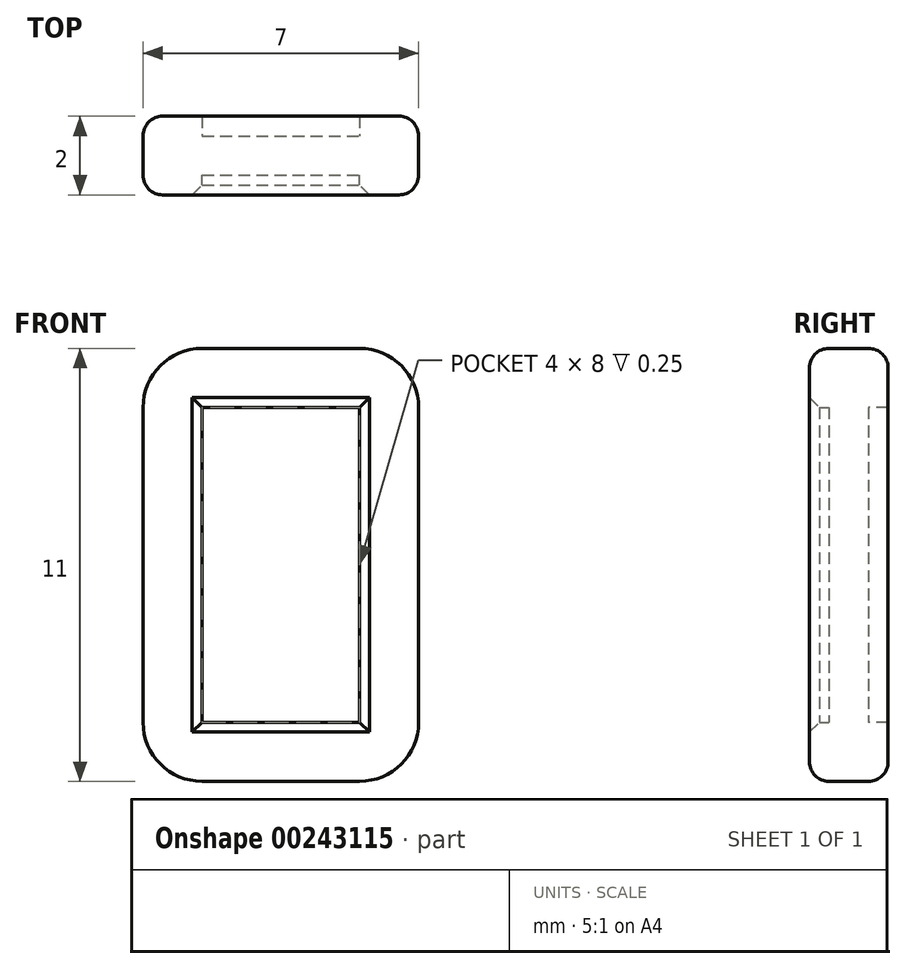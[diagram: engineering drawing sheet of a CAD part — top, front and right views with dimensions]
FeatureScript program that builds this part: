
annotation { "Feature Type Name" : "Feature", "Feature Type Description" : "" }
export const myFeature = defineFeature(function(context is Context, id is Id, definition is map)
    precondition{}
    {
        {
            var Q0;
            Q0=qCreatedBy(makeId("Front.planeOp"),FACE);
            var sketch = newSketch(context, id + "F0", { "sketchPlane" : qUnion([Q0])});
            skLineSegment(sketch, "E0", {"start": v(0, 0) * mm, "end": v(6, 0) * mm});
            skLineSegment(sketch, "E1", {"start": v(6, 0) * mm, "end": v(6, 10) * mm});
            skLineSegment(sketch, "E2", {"start": v(6, 10) * mm, "end": v(0, 10) * mm});
            skLineSegment(sketch, "E3", {"start": v(0, 10) * mm, "end": v(0, 0) * mm});
            skSolve(sketch);
        }
        {
            var Q0;
            Q0=makeQuery(id+"F0.imprint","IMPRINT",FACE,{"disambiguationData":[TD([[makeQuery(id+"F0.imprint","IMPRINT",EDGE,{"derivedFrom":sQuery(id+"F0.wireOp",EDGE,"E0")}),1.0]])]});
            extrude(context, id + "F1", {"entities" : qUnion([Q0]), "depth" : 1 * mm});
        }
        {
            var Q0;
            Q0=makeQuery(id+"F1.opExtrude","SWEPT_EDGE",EDGE,{"disambiguationData":[OSD([sQuery(id+"F0.wireOp",EDGE,"E2"),sQuery(id+"F0.wireOp",EDGE,"E3")])]});
            var Q1;
            Q1=makeQuery(id+"F1.opExtrude","SWEPT_EDGE",EDGE,{"disambiguationData":[OSD([sQuery(id+"F0.wireOp",EDGE,"E0"),sQuery(id+"F0.wireOp",EDGE,"E3")])]});
            var Q2;
            Q2=makeQuery(id+"F1.opExtrude","SWEPT_EDGE",EDGE,{"disambiguationData":[OSD([sQuery(id+"F0.wireOp",EDGE,"E0"),sQuery(id+"F0.wireOp",EDGE,"E1")])]});
            var Q3;
            Q3=makeQuery(id+"F1.opExtrude","SWEPT_EDGE",EDGE,{"disambiguationData":[OSD([sQuery(id+"F0.wireOp",EDGE,"E1"),sQuery(id+"F0.wireOp",EDGE,"E2")])]});
            fillet(context, id + "F2", {"entities" : qUnion([Q0, Q1, Q2, Q3]), "radius" : 1 * mm, "tangentPropagation" : true, "allowEdgeOverflow" : false});
        }
        {
            var Q0;
            Q0=qCreatedBy(makeId("Top.planeOp"),FACE);
            cPlane(context, id + "F3", {"entities" : qUnion([Q0]), "cplaneType" : CPlaneType.OFFSET, "offset" : 1 * mm, "width" : 150 * mm, "height" : 150 * mm});
        }
        {
            var Q0;
            Q0=qCreatedBy(id+"F3.planeOp",FACE);
            var sketch = newSketch(context, id + "F4", { "sketchPlane" : qUnion([Q0])});
            skPoint(sketch, "E4.0", {"position": v(6, -1) * mm});
            skPoint(sketch, "E4.1", {"position": v(6, 0) * mm});
            skPoint(sketch, "E4.2", {"position": v(5, -1) * mm});
            skPoint(sketch, "E4.3", {"position": v(5, 0) * mm});
            skLineSegment(sketch, "E5", {"start": v(5, -1) * mm, "end": v(6, -1) * mm});
            skLineSegment(sketch, "E6", {"start": v(6, 0) * mm, "end": v(6, -1) * mm});
            skLineSegment(sketch, "E7", {"start": v(6, 0) * mm, "end": v(5, 0) * mm});
            skLineSegment(sketch, "E8.0", {"start": v(6.5, 0.5) * mm, "end": v(5, 0.5) * mm});
            skLineSegment(sketch, "E8.1", {"start": v(6.5, 0.5) * mm, "end": v(6.5, -1.5) * mm});
            skLineSegment(sketch, "E8.2", {"start": v(5, -1.5) * mm, "end": v(6.5, -1.5) * mm});
            skLineSegment(sketch, "E9", {"start": v(5, -1.5) * mm, "end": v(5, -1) * mm});
            skLineSegment(sketch, "E10", {"start": v(5, 0.5) * mm, "end": v(5, 0) * mm});
            skSolve(sketch);
        }
        {
            var Q0;
            Q0=makeQuery(id+"F4.imprint","IMPRINT",FACE,{"disambiguationData":[TD([[makeQuery(id+"F4.imprint","IMPRINT",EDGE,{"derivedFrom":sQuery(id+"F4.wireOp",EDGE,"E5")}),-1.0]])]});
            var Q1;
            Q1=makeQuery(id+"F1.opExtrude","CAP_EDGE",EDGE,{"disambiguationData":[OSD([sQuery(id+"F0.wireOp",EDGE,"E1")])],"isStart":false});
            var Q2;
            {var subQ0=sQuery(id+"F0.wireOp",EDGE,"E2");var subQ1=sQuery(id+"F0.wireOp",EDGE,"E1");Q2=makeQuery(id+"F2.opFillet","BLEND_EDGE",EDGE,{"blendedFrom":[makeQuery(id+"F1.opExtrude","SWEPT_EDGE",EDGE,{"disambiguationData":[OSD([subQ1,subQ0])]}),makeQuery(id+"F1.opExtrude","CAP_FACE",FACE,{"disambiguationData":[OSD([sQuery(id+"F0.wireOp",EDGE,"E0"),subQ1,subQ0,sQuery(id+"F0.wireOp",EDGE,"E3")])],"isStart":false})],"blendedInto":[makeQuery(id+"F1.opExtrude","CAP_FACE",FACE,{"disambiguationData":[OSD([sQuery(id+"F0.wireOp",EDGE,"E0"),subQ1,subQ0,sQuery(id+"F0.wireOp",EDGE,"E3")])],"isStart":false})]});}
            var Q3;
            Q3=makeQuery(id+"F1.opExtrude","CAP_EDGE",EDGE,{"disambiguationData":[OSD([sQuery(id+"F0.wireOp",EDGE,"E2")])],"isStart":false});
            var Q4;
            {var subQ0=sQuery(id+"F0.wireOp",EDGE,"E3");var subQ1=sQuery(id+"F0.wireOp",EDGE,"E2");Q4=makeQuery(id+"F2.opFillet","BLEND_EDGE",EDGE,{"blendedFrom":[makeQuery(id+"F1.opExtrude","SWEPT_EDGE",EDGE,{"disambiguationData":[OSD([subQ1,subQ0])]}),makeQuery(id+"F1.opExtrude","CAP_FACE",FACE,{"disambiguationData":[OSD([sQuery(id+"F0.wireOp",EDGE,"E0"),sQuery(id+"F0.wireOp",EDGE,"E1"),subQ1,subQ0])],"isStart":false})],"blendedInto":[makeQuery(id+"F1.opExtrude","CAP_FACE",FACE,{"disambiguationData":[OSD([sQuery(id+"F0.wireOp",EDGE,"E0"),sQuery(id+"F0.wireOp",EDGE,"E1"),subQ1,subQ0])],"isStart":false})]});}
            var Q5;
            Q5=makeQuery(id+"F1.opExtrude","CAP_EDGE",EDGE,{"disambiguationData":[OSD([sQuery(id+"F0.wireOp",EDGE,"E3")])],"isStart":false});
            var Q6;
            {var subQ0=sQuery(id+"F0.wireOp",EDGE,"E3");var subQ1=sQuery(id+"F0.wireOp",EDGE,"E0");Q6=makeQuery(id+"F2.opFillet","BLEND_EDGE",EDGE,{"blendedFrom":[makeQuery(id+"F1.opExtrude","SWEPT_EDGE",EDGE,{"disambiguationData":[OSD([subQ1,subQ0])]}),makeQuery(id+"F1.opExtrude","CAP_FACE",FACE,{"disambiguationData":[OSD([subQ1,sQuery(id+"F0.wireOp",EDGE,"E1"),sQuery(id+"F0.wireOp",EDGE,"E2"),subQ0])],"isStart":false})],"blendedInto":[makeQuery(id+"F1.opExtrude","CAP_FACE",FACE,{"disambiguationData":[OSD([subQ1,sQuery(id+"F0.wireOp",EDGE,"E1"),sQuery(id+"F0.wireOp",EDGE,"E2"),subQ0])],"isStart":false})]});}
            var Q7;
            Q7=makeQuery(id+"F1.opExtrude","CAP_EDGE",EDGE,{"disambiguationData":[OSD([sQuery(id+"F0.wireOp",EDGE,"E0")])],"isStart":false});
            var Q8;
            {var subQ0=sQuery(id+"F0.wireOp",EDGE,"E1");var subQ1=sQuery(id+"F0.wireOp",EDGE,"E0");Q8=makeQuery(id+"F2.opFillet","BLEND_EDGE",EDGE,{"blendedFrom":[makeQuery(id+"F1.opExtrude","SWEPT_EDGE",EDGE,{"disambiguationData":[OSD([subQ1,subQ0])]}),makeQuery(id+"F1.opExtrude","CAP_FACE",FACE,{"disambiguationData":[OSD([subQ1,subQ0,sQuery(id+"F0.wireOp",EDGE,"E2"),sQuery(id+"F0.wireOp",EDGE,"E3")])],"isStart":false})],"blendedInto":[makeQuery(id+"F1.opExtrude","CAP_FACE",FACE,{"disambiguationData":[OSD([subQ1,subQ0,sQuery(id+"F0.wireOp",EDGE,"E2"),sQuery(id+"F0.wireOp",EDGE,"E3")])],"isStart":false})]});}
            sweep(context, id + "F5", {"operationType" : NewBodyOperationType.ADD, "profiles" : qUnion([Q0]), "path" : qUnion([Q1, Q2, Q3, Q4, Q5, Q6, Q7, Q8])});
        }
        {
            var Q0;
            {var subQ0=sQuery(id+"F4.wireOp",EDGE,"E8.2");var subQ1=sQuery(id+"F4.wireOp",EDGE,"E8.1");var subQ2=sQuery(id+"F0.wireOp",EDGE,"E3");var subQ3=sQuery(id+"F0.wireOp",EDGE,"E2");var subQ4=sQuery(id+"F0.wireOp",EDGE,"E1");var subQ5=sQuery(id+"F0.wireOp",EDGE,"E0");Q0=makeQuery(id+"F5.opSweep","SWEPT_EDGE",EDGE,{"disambiguationData":[OSD([subQ5,subQ4,subQ3,subQ2,subQ1,subQ0]),TDD([makeQuery(id+"F2.opFillet","BLEND_EDGE",EDGE,{"blendedFrom":[makeQuery(id+"F1.opExtrude","SWEPT_EDGE",EDGE,{"disambiguationData":[OSD([subQ4,subQ3])]}),makeQuery(id+"F1.opExtrude","CAP_FACE",FACE,{"disambiguationData":[OSD([subQ5,subQ4,subQ3,subQ2])],"isStart":false})],"blendedInto":[makeQuery(id+"F1.opExtrude","CAP_FACE",FACE,{"disambiguationData":[OSD([subQ5,subQ4,subQ3,subQ2])],"isStart":false})]}),makeQuery(id+"F4.imprint","INTERSECT",VERTEX,{"derivedFrom":[subQ1,subQ0]})])]});}
            var Q1;
            {var subQ0=sQuery(id+"F4.wireOp",EDGE,"E8.1");var subQ1=sQuery(id+"F4.wireOp",EDGE,"E8.0");var subQ2=sQuery(id+"F0.wireOp",EDGE,"E3");var subQ3=sQuery(id+"F0.wireOp",EDGE,"E2");var subQ4=sQuery(id+"F0.wireOp",EDGE,"E1");var subQ5=sQuery(id+"F0.wireOp",EDGE,"E0");Q1=makeQuery(id+"F5.opSweep","SWEPT_EDGE",EDGE,{"disambiguationData":[OSD([subQ5,subQ4,subQ3,subQ2,subQ1,subQ0]),TDD([makeQuery(id+"F2.opFillet","BLEND_EDGE",EDGE,{"blendedFrom":[makeQuery(id+"F1.opExtrude","SWEPT_EDGE",EDGE,{"disambiguationData":[OSD([subQ4,subQ3])]}),makeQuery(id+"F1.opExtrude","CAP_FACE",FACE,{"disambiguationData":[OSD([subQ5,subQ4,subQ3,subQ2])],"isStart":false})],"blendedInto":[makeQuery(id+"F1.opExtrude","CAP_FACE",FACE,{"disambiguationData":[OSD([subQ5,subQ4,subQ3,subQ2])],"isStart":false})]}),makeQuery(id+"F4.imprint","INTERSECT",VERTEX,{"derivedFrom":[subQ1,subQ0]})])]});}
            var Q2;
            {var subQ0=sQuery(id+"F4.wireOp",EDGE,"E8.2");var subQ1=sQuery(id+"F4.wireOp",EDGE,"E8.1");var subQ2=sQuery(id+"F0.wireOp",EDGE,"E3");var subQ3=sQuery(id+"F0.wireOp",EDGE,"E2");var subQ4=sQuery(id+"F0.wireOp",EDGE,"E1");var subQ5=sQuery(id+"F0.wireOp",EDGE,"E0");Q2=makeQuery(id+"F5.opSweep","SWEPT_EDGE",EDGE,{"disambiguationData":[OSD([subQ5,subQ4,subQ3,subQ2,subQ1,subQ0]),TDD([makeQuery(id+"F2.opFillet","BLEND_EDGE",EDGE,{"blendedFrom":[makeQuery(id+"F1.opExtrude","SWEPT_EDGE",EDGE,{"disambiguationData":[OSD([subQ3,subQ2])]}),makeQuery(id+"F1.opExtrude","CAP_FACE",FACE,{"disambiguationData":[OSD([subQ5,subQ4,subQ3,subQ2])],"isStart":false})],"blendedInto":[makeQuery(id+"F1.opExtrude","CAP_FACE",FACE,{"disambiguationData":[OSD([subQ5,subQ4,subQ3,subQ2])],"isStart":false})]}),makeQuery(id+"F4.imprint","INTERSECT",VERTEX,{"derivedFrom":[subQ1,subQ0]})])]});}
            var Q3;
            {var subQ0=sQuery(id+"F4.wireOp",EDGE,"E8.1");var subQ1=sQuery(id+"F0.wireOp",EDGE,"E3");var subQ2=sQuery(id+"F0.wireOp",EDGE,"E2");var subQ3=sQuery(id+"F0.wireOp",EDGE,"E1");var subQ4=sQuery(id+"F0.wireOp",EDGE,"E0");Q3=makeQuery(id+"F5.opSweep","SWEPT_FACE",FACE,{"disambiguationData":[OSD([subQ4,subQ3,subQ2,subQ1,subQ0]),TDD([makeQuery(id+"F2.opFillet","BLEND_EDGE",EDGE,{"blendedFrom":[makeQuery(id+"F1.opExtrude","SWEPT_EDGE",EDGE,{"disambiguationData":[OSD([subQ2,subQ1])]}),makeQuery(id+"F1.opExtrude","CAP_FACE",FACE,{"disambiguationData":[OSD([subQ4,subQ3,subQ2,subQ1])],"isStart":false})],"blendedInto":[makeQuery(id+"F1.opExtrude","CAP_FACE",FACE,{"disambiguationData":[OSD([subQ4,subQ3,subQ2,subQ1])],"isStart":false})]}),makeQuery(id+"F4.imprint","IMPRINT",EDGE,{"derivedFrom":subQ0})])]});}
            var Q4;
            {var subQ0=sQuery(id+"F4.wireOp",EDGE,"E8.2");var subQ1=sQuery(id+"F4.wireOp",EDGE,"E8.1");var subQ2=sQuery(id+"F0.wireOp",EDGE,"E3");var subQ3=sQuery(id+"F0.wireOp",EDGE,"E2");var subQ4=sQuery(id+"F0.wireOp",EDGE,"E1");var subQ5=sQuery(id+"F0.wireOp",EDGE,"E0");Q4=makeQuery(id+"F5.opSweep","SWEPT_EDGE",EDGE,{"disambiguationData":[OSD([subQ5,subQ4,subQ3,subQ2,subQ1,subQ0]),TDD([makeQuery(id+"F2.opFillet","BLEND_EDGE",EDGE,{"blendedFrom":[makeQuery(id+"F1.opExtrude","SWEPT_EDGE",EDGE,{"disambiguationData":[OSD([subQ5,subQ4])]}),makeQuery(id+"F1.opExtrude","CAP_FACE",FACE,{"disambiguationData":[OSD([subQ5,subQ4,subQ3,subQ2])],"isStart":false})],"blendedInto":[makeQuery(id+"F1.opExtrude","CAP_FACE",FACE,{"disambiguationData":[OSD([subQ5,subQ4,subQ3,subQ2])],"isStart":false})]}),makeQuery(id+"F4.imprint","INTERSECT",VERTEX,{"derivedFrom":[subQ1,subQ0]})])]});}
            var Q5;
            {var subQ0=sQuery(id+"F4.wireOp",EDGE,"E8.1");var subQ1=sQuery(id+"F4.wireOp",EDGE,"E8.0");var subQ2=sQuery(id+"F0.wireOp",EDGE,"E3");var subQ3=sQuery(id+"F0.wireOp",EDGE,"E2");var subQ4=sQuery(id+"F0.wireOp",EDGE,"E1");var subQ5=sQuery(id+"F0.wireOp",EDGE,"E0");Q5=makeQuery(id+"F5.opSweep","SWEPT_EDGE",EDGE,{"disambiguationData":[OSD([subQ5,subQ4,subQ3,subQ2,subQ1,subQ0]),TDD([makeQuery(id+"F2.opFillet","BLEND_EDGE",EDGE,{"blendedFrom":[makeQuery(id+"F1.opExtrude","SWEPT_EDGE",EDGE,{"disambiguationData":[OSD([subQ5,subQ4])]}),makeQuery(id+"F1.opExtrude","CAP_FACE",FACE,{"disambiguationData":[OSD([subQ5,subQ4,subQ3,subQ2])],"isStart":false})],"blendedInto":[makeQuery(id+"F1.opExtrude","CAP_FACE",FACE,{"disambiguationData":[OSD([subQ5,subQ4,subQ3,subQ2])],"isStart":false})]}),makeQuery(id+"F4.imprint","INTERSECT",VERTEX,{"derivedFrom":[subQ1,subQ0]})])]});}
            var Q6;
            Q6=makeQuery(id+"F5.opSweep","MID_CAP_EDGE",EDGE,{"disambiguationData":[OSD([sQuery(id+"F0.wireOp",EDGE,"E0"),sQuery(id+"F0.wireOp",EDGE,"E1"),sQuery(id+"F0.wireOp",EDGE,"E2"),sQuery(id+"F0.wireOp",EDGE,"E3"),sQuery(id+"F4.wireOp",EDGE,"E8.1")])],"capPos":4.0});
            var Q7;
            {var subQ0=sQuery(id+"F4.wireOp",EDGE,"E8.1");var subQ1=sQuery(id+"F0.wireOp",EDGE,"E3");var subQ2=sQuery(id+"F0.wireOp",EDGE,"E2");var subQ3=sQuery(id+"F0.wireOp",EDGE,"E1");var subQ4=sQuery(id+"F0.wireOp",EDGE,"E0");Q7=makeQuery(id+"F5.opSweep","SWEPT_FACE",FACE,{"disambiguationData":[OSD([subQ4,subQ3,subQ2,subQ1,subQ0]),TDD([makeQuery(id+"F2.opFillet","BLEND_EDGE",EDGE,{"blendedFrom":[makeQuery(id+"F1.opExtrude","SWEPT_EDGE",EDGE,{"disambiguationData":[OSD([subQ4,subQ1])]}),makeQuery(id+"F1.opExtrude","CAP_FACE",FACE,{"disambiguationData":[OSD([subQ4,subQ3,subQ2,subQ1])],"isStart":false})],"blendedInto":[makeQuery(id+"F1.opExtrude","CAP_FACE",FACE,{"disambiguationData":[OSD([subQ4,subQ3,subQ2,subQ1])],"isStart":false})]}),makeQuery(id+"F4.imprint","IMPRINT",EDGE,{"derivedFrom":subQ0})])]});}
            fillet(context, id + "F6", {"entities" : qUnion([Q0, Q1, Q2, Q3, Q4, Q5, Q6, Q7]), "radius" : 0.5 * mm, "tangentPropagation" : true, "allowEdgeOverflow" : false});
        }
        {
            var Q0;
            Q0=makeQuery(id+"F5.opSweep","SWEPT_EDGE",EDGE,{"disambiguationData":[OSD([sQuery(id+"F0.wireOp",EDGE,"E2"),sQuery(id+"F4.wireOp",EDGE,"E8.2"),sQuery(id+"F4.wireOp",EDGE,"E9")])]});
            var Q1;
            Q1=makeQuery(id+"F5.opSweep","SWEPT_EDGE",EDGE,{"disambiguationData":[OSD([sQuery(id+"F0.wireOp",EDGE,"E1"),sQuery(id+"F4.wireOp",EDGE,"E8.2"),sQuery(id+"F4.wireOp",EDGE,"E9")])]});
            var Q2;
            Q2=makeQuery(id+"F5.opSweep","SWEPT_EDGE",EDGE,{"disambiguationData":[OSD([sQuery(id+"F0.wireOp",EDGE,"E3"),sQuery(id+"F4.wireOp",EDGE,"E8.2"),sQuery(id+"F4.wireOp",EDGE,"E9")])]});
            var Q3;
            Q3=makeQuery(id+"F5.opSweep","SWEPT_EDGE",EDGE,{"disambiguationData":[OSD([sQuery(id+"F0.wireOp",EDGE,"E0"),sQuery(id+"F4.wireOp",EDGE,"E8.2"),sQuery(id+"F4.wireOp",EDGE,"E9")])]});
            chamfer(context, id + "F7", {"entities" : qUnion([Q0, Q1, Q2, Q3]), "width" : 0.25 * mm, "tangentPropagation" : true});
        }
    });
